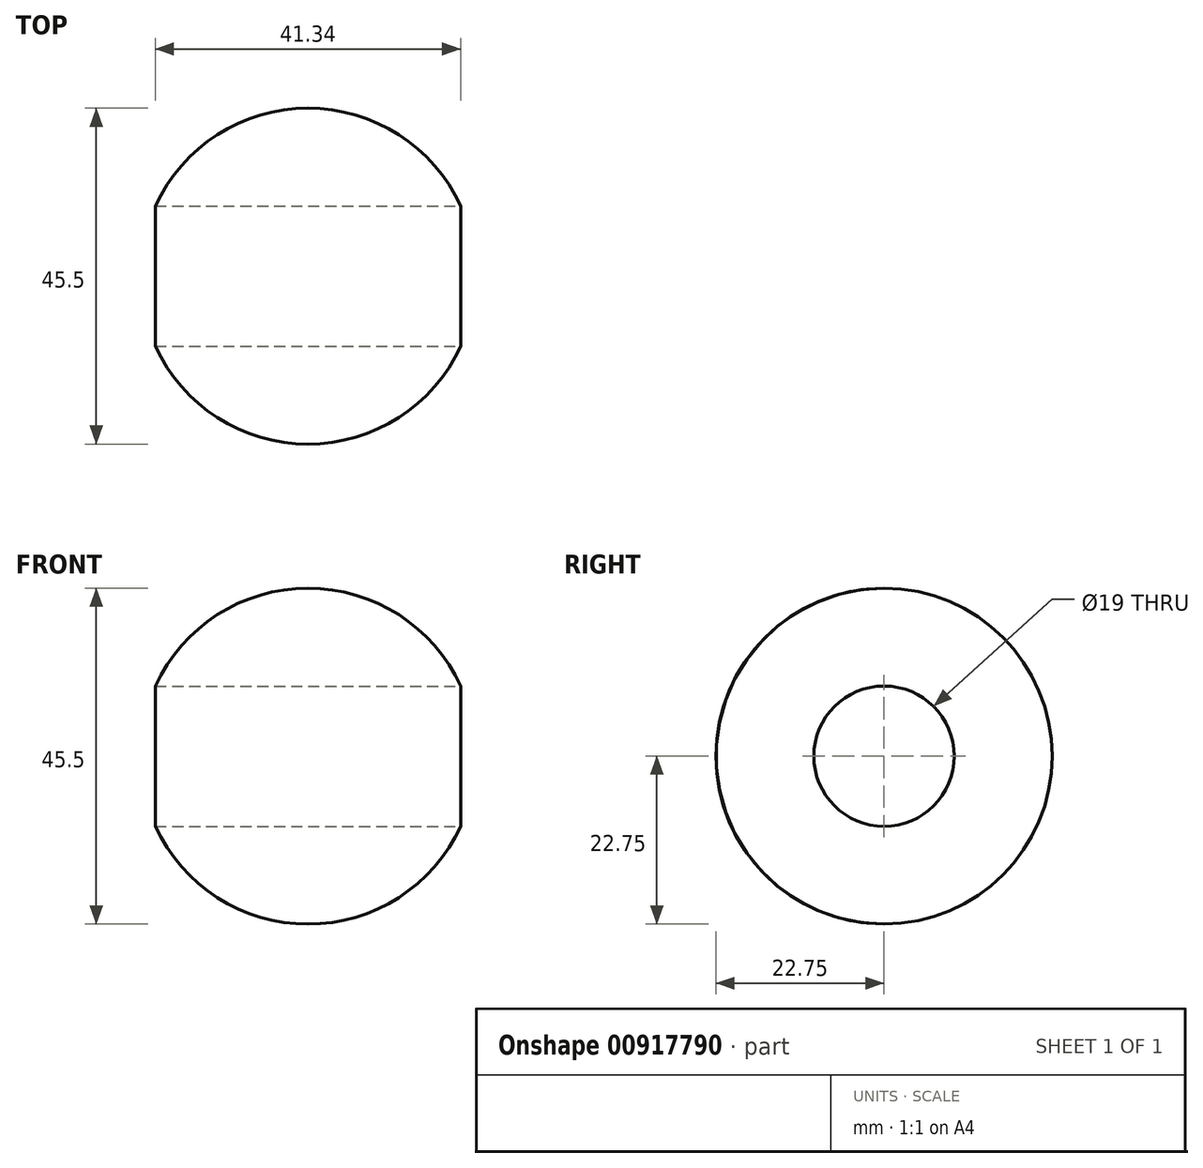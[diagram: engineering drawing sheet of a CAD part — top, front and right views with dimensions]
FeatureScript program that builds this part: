
annotation { "Feature Type Name" : "Feature", "Feature Type Description" : "" }
export const myFeature = defineFeature(function(context is Context, id is Id, definition is map)
    precondition{}
    {
        {
            var Q0;
            Q0=qCreatedBy(makeId("Front.planeOp"),FACE);
            var sketch = newSketch(context, id + "F0", { "sketchPlane" : qUnion([Q0])});
            skArc(sketch, "E0", {"start": v(0, -22.75) * mm, "mid": v(22.75, 0) * mm, "end": v(0, 22.75) * mm});
            skLineSegment(sketch, "E1", {"start": v(0, 22.75) * mm, "end": v(0, -22.75) * mm});
            skSolve(sketch);
        }
        {
            var Q0;
            Q0=makeQuery(id+"F0.imprint","IMPRINT",FACE,{"disambiguationData":[TD([[makeQuery(id+"F0.imprint","IMPRINT",EDGE,{"derivedFrom":sQuery(id+"F0.wireOp",EDGE,"E0")}),1.0]])]});
            var Q1;
            Q1=sQuery(id+"F0.wireOp",EDGE,"E1");
            revolve(context, id + "F1", {"surfaceOperationType" : NewSurfaceOperationType.NEW, "entities" : qUnion([Q0]), "axis" : qUnion([Q1]), "revolveType" : RevolveType.FULL});
        }
        {
            var Q0;
            Q0=qCreatedBy(makeId("Right.planeOp"),FACE);
            var sketch = newSketch(context, id + "F2", { "sketchPlane" : qUnion([Q0])});
            skCircle(sketch, "E2", {"center": v(0, 0) * mm, "radius": 9.5 * mm});
            skSolve(sketch);
        }
        {
            var Q0;
            Q0 = qSketchRegion(id + "F2", true);
            extrude(context, id + "F3", {"entities" : qUnion([Q0]), "operationType" : NewBodyOperationType.REMOVE, "endBound" : BoundingType.SYMMETRIC, "oppositeDirection" : true, "depth" : 60 * mm, "offsetDistance" : 25 * mm});
        }
    });
